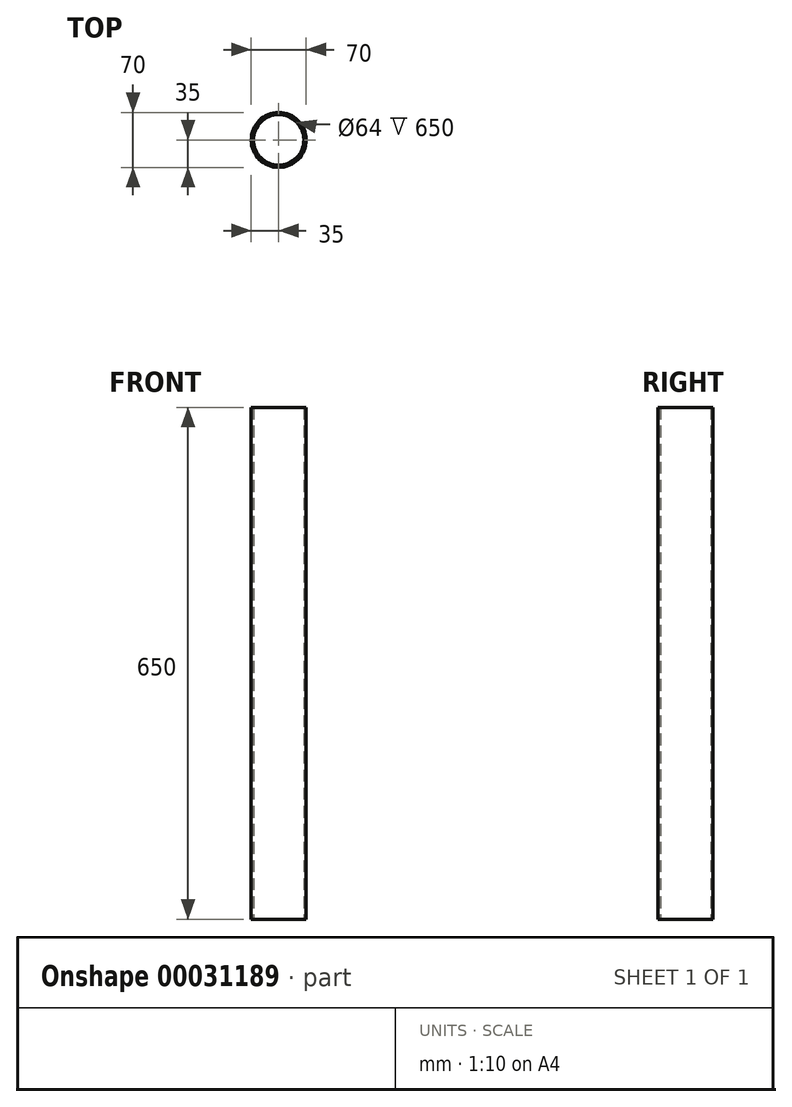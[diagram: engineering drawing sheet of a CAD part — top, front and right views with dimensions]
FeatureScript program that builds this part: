
annotation { "Feature Type Name" : "Feature", "Feature Type Description" : "" }
export const myFeature = defineFeature(function(context is Context, id is Id, definition is map)
    precondition{}
    {
        {
            var Q0;
            Q0=qCreatedBy(makeId("Top.planeOp"),FACE);
            var sketch = newSketch(context, id + "F0", { "sketchPlane" : qUnion([Q0])});
            skCircle(sketch, "E0", {"center": v(0, 0) * mm, "radius": 35 * mm});
            skCircle(sketch, "E1.0", {"center": v(0, 0) * mm, "radius": 32 * mm});
            skSolve(sketch);
        }
        {
            var Q0;
            Q0=makeQuery(id+"F0.imprint","IMPRINT",FACE,{"disambiguationData":[TD([[makeQuery(id+"F0.imprint","IMPRINT",EDGE,{"derivedFrom":sQuery(id+"F0.wireOp",EDGE,"E0")}),1.0]])]});
            extrude(context, id + "F1", {"entities" : qUnion([Q0]), "depth" : 650 * mm});
        }
    });
